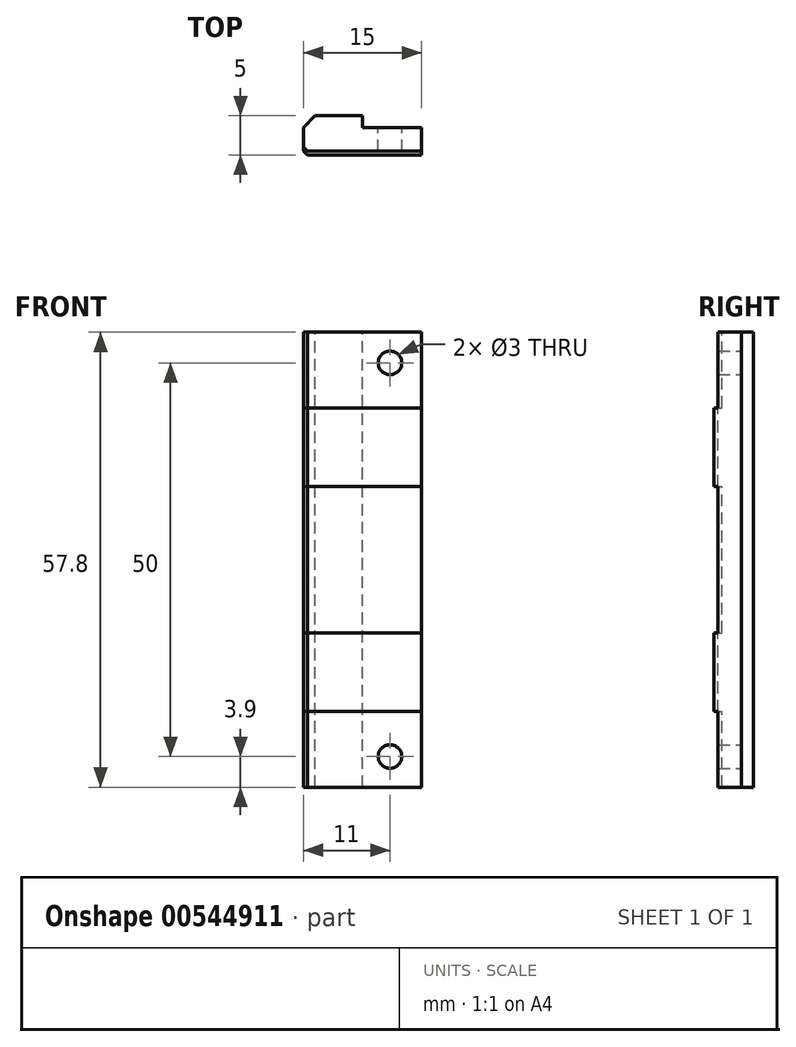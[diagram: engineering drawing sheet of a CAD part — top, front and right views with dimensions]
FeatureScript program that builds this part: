
annotation { "Feature Type Name" : "Feature", "Feature Type Description" : "" }
export const myFeature = defineFeature(function(context is Context, id is Id, definition is map)
    precondition{}
    {
        {
            var Q0;
            Q0=qCreatedBy(makeId("Right.planeOp"),FACE);
            var sketch = newSketch(context, id + "F0", { "sketchPlane" : qUnion([Q0])});
            skLineSegment(sketch, "E0", {"start": v(0, 28.9) * mm, "end": v(3, 28.9) * mm});
            skLineSegment(sketch, "E1", {"start": v(3, 28.9) * mm, "end": v(3, -28.9) * mm});
            skLineSegment(sketch, "E2", {"start": v(3, -28.9) * mm, "end": v(0, -28.9) * mm});
            skLineSegment(sketch, "E3", {"start": v(0, 28.9) * mm, "end": v(0, 24.9) * mm});
            skLineSegment(sketch, "E4", {"start": v(0, 24.9) * mm, "end": v(0, 24.9) * mm});
            skLineSegment(sketch, "E5", {"start": v(0, 24.9) * mm, "end": v(0, -24.9) * mm});
            skLineSegment(sketch, "E6", {"start": v(0, -24.9) * mm, "end": v(0, -24.9) * mm});
            skLineSegment(sketch, "E7", {"start": v(0, -24.9) * mm, "end": v(0, -28.9) * mm});
            skSolve(sketch);
        }
        {
            var Q0;
            Q0=qSketchRegion(id+"F0",true);
            extrude(context, id + "F1", {"entities" : qUnion([Q0]), "depth" : 7.5 * mm, "hasSecondDirection" : true, "secondDirectionOppositeDirection" : true, "secondDirectionDepth" : 7.5 * mm});
        }
        {
            var Q0;
            Q0=makeQuery(id+"F1.opExtrude","SWEPT_FACE",FACE,{"disambiguationData":[OSD([sQuery(id+"F0.wireOp",EDGE,"E1")])]});
            var sketch = newSketch(context, id + "F2", { "sketchPlane" : qUnion([Q0])});
            skCircle(sketch, "E8", {"center": v(-3.5, 25) * mm, "radius": 1.5 * mm});
            skCircle(sketch, "E9", {"center": v(-3.5, -25) * mm, "radius": 1.5 * mm});
            skSolve(sketch);
        }
        {
            var Q0;
            Q0=makeQuery(id+"F1.opExtrude","SWEPT_FACE",FACE,{"disambiguationData":[OSD([sQuery(id+"F0.wireOp",EDGE,"E2")])]});
            var sketch = newSketch(context, id + "F3", { "sketchPlane" : qUnion([Q0])});
            skCircle(sketch, "E10", {"center": v(0, -60) * mm, "radius": 2.5 * mm});
            skSolve(sketch);
        }
        {
            var Q0;
            Q0=qSketchRegion(id+"F3",true);
            extrude(context, id + "F4", {"entities" : qUnion([Q0]), "operationType" : NewBodyOperationType.REMOVE, "oppositeDirection" : true, "depth" : 100 * mm});
        }
        {
            var Q0;
            Q0=makeQuery(id+"F1.opExtrude","SWEPT_FACE",FACE,{"disambiguationData":[OSD([sQuery(id+"F0.wireOp",EDGE,"E1")])]});
            var sketch = newSketch(context, id + "F5", { "sketchPlane" : qUnion([Q0])});
            skCircle(sketch, "E11", {"center": v(-3.5, 31) * mm, "radius": 1.5 * mm});
            skCircle(sketch, "E12", {"center": v(-3.5, -31) * mm, "radius": 1.5 * mm});
            skSolve(sketch);
        }
        {
            var Q0;
            Q0=makeQuery(id+"F1.opExtrude","CAP_FACE",FACE,{"disambiguationData":[OSD([sQuery(id+"F0.wireOp",EDGE,"E0"),sQuery(id+"F0.wireOp",EDGE,"E1"),sQuery(id+"F0.wireOp",EDGE,"E2"),sQuery(id+"F0.wireOp",EDGE,"E3"),sQuery(id+"F0.wireOp",EDGE,"E5"),sQuery(id+"F0.wireOp",EDGE,"E7")])],"isStart":false});
            var sketch = newSketch(context, id + "F6", { "sketchPlane" : qUnion([Q0])});
            skLineSegment(sketch, "E13.bottom", {"start": v(0, 19.29) * mm, "end": v(-0.5, 19.29) * mm});
            skLineSegment(sketch, "E13.top", {"start": v(0, 9.29) * mm, "end": v(-0.5, 9.29) * mm});
            skLineSegment(sketch, "E13.left", {"start": v(0, 19.29) * mm, "end": v(0, 9.29) * mm});
            skLineSegment(sketch, "E13.right", {"start": v(-0.5, 19.29) * mm, "end": v(-0.5, 9.29) * mm});
            skLineSegment(sketch, "E14.bottom", {"start": v(0, -9.29) * mm, "end": v(-0.5, -9.29) * mm});
            skLineSegment(sketch, "E14.top", {"start": v(0, -19.29) * mm, "end": v(-0.5, -19.29) * mm});
            skLineSegment(sketch, "E14.left", {"start": v(0, -9.29) * mm, "end": v(0, -19.29) * mm});
            skLineSegment(sketch, "E14.right", {"start": v(-0.5, -9.29) * mm, "end": v(-0.5, -19.29) * mm});
            skLineSegment(sketch, "E15", {"start": v(-19.13, -14.29) * mm, "end": v(16.5, -14.29) * mm, "construction": true});
            skPoint(sketch, "E15.startSnap0", {"position": v(-0.5, -14.29) * mm});
            skLineSegment(sketch, "E16", {"start": v(-17.07, 14.29) * mm, "end": v(17.48, 14.29) * mm, "construction": true});
            skPoint(sketch, "E16.startSnap0", {"position": v(-0.5, 14.29) * mm});
            skSolve(sketch);
        }
        {
            var Q0;
            Q0=qSketchRegion(id+"F6",true);
            var Q1;
            Q1=makeQuery(id+"F1.opExtrude","CAP_FACE",FACE,{"disambiguationData":[OSD([sQuery(id+"F0.wireOp",EDGE,"E0"),sQuery(id+"F0.wireOp",EDGE,"E1"),sQuery(id+"F0.wireOp",EDGE,"E2"),sQuery(id+"F0.wireOp",EDGE,"E3"),sQuery(id+"F0.wireOp",EDGE,"E5"),sQuery(id+"F0.wireOp",EDGE,"E7")])],"isStart":true});
            extrude(context, id + "F7", {"entities" : qUnion([Q0]), "operationType" : NewBodyOperationType.ADD, "endBound" : BoundingType.UP_TO_SURFACE, "oppositeDirection" : true, "endBoundEntityFace" : qUnion([Q1]), "depth" : 25 * mm});
        }
        {
            var Q0;
            Q0=makeQuery(id+"Fmcx1tmVuyddfUs_2.boolean.opBoolean","MERGE",FACE,{"derivedFrom":[makeQuery(id+"F1.opExtrude","SWEPT_FACE",FACE,{"disambiguationData":[OSD([sQuery(id+"F0.wireOp",EDGE,"E1")])]}),makeQuery(id+"Fmcx1tmVuyddfUs_2.opExtrude","CAP_FACE",FACE,{"disambiguationData":[OSD([sQuery(id+"FtdUe9tOK60J6PF_2.wireOp",EDGE,"JsNW8nu7-rLeb-dfcb-XSDR-FWr7f3ZU8y3m.bottom"),sQuery(id+"FtdUe9tOK60J6PF_2.wireOp",EDGE,"JsNW8nu7-rLeb-dfcb-XSDR-FWr7f3ZU8y3m.top"),sQuery(id+"FtdUe9tOK60J6PF_2.wireOp",EDGE,"JsNW8nu7-rLeb-dfcb-XSDR-FWr7f3ZU8y3m.left"),sQuery(id+"FtdUe9tOK60J6PF_2.wireOp",EDGE,"JsNW8nu7-rLeb-dfcb-XSDR-FWr7f3ZU8y3m.right")])],"isStart":true}),makeQuery(id+"Fmcx1tmVuyddfUs_2.opExtrude","CAP_FACE",FACE,{"disambiguationData":[OSD([sQuery(id+"FtdUe9tOK60J6PF_2.wireOp",EDGE,"ceRr9AZa-OO9h-L4Fo-6wB5-B8ZzmuX6AbRb.bottom"),sQuery(id+"FtdUe9tOK60J6PF_2.wireOp",EDGE,"ceRr9AZa-OO9h-L4Fo-6wB5-B8ZzmuX6AbRb.top"),sQuery(id+"FtdUe9tOK60J6PF_2.wireOp",EDGE,"ceRr9AZa-OO9h-L4Fo-6wB5-B8ZzmuX6AbRb.left"),sQuery(id+"FtdUe9tOK60J6PF_2.wireOp",EDGE,"ceRr9AZa-OO9h-L4Fo-6wB5-B8ZzmuX6AbRb.right")])],"isStart":true})]});
            var sketch = newSketch(context, id + "F8", { "sketchPlane" : qUnion([Q0])});
            skLineSegment(sketch, "E17", {"start": v(0, -35.02) * mm, "end": v(0, 28.9) * mm});
            skSolve(sketch);
        }
        {
            var Q0;
            Q0=qSketchRegion(id+"F2",true);
            extrude(context, id + "F9", {"entities" : qUnion([Q0]), "operationType" : NewBodyOperationType.REMOVE, "oppositeDirection" : true, "depth" : 25 * mm});
        }
        {
            var Q0;
            {var subQ4=sQuery(id+"FtdUe9tOK60J6PF_2.wireOp",EDGE,"JsNW8nu7-rLeb-dfcb-XSDR-FWr7f3ZU8y3m.right");var subQ5=makeQuery(id+"Fmcx1tmVuyddfUs_2.opExtrude","CAP_EDGE",EDGE,{"disambiguationData":[OSD([subQ4])],"isStart":true});Q0=makeQuery(id+"F8.imprint","IMPRINT",FACE,{"disambiguationData":[TD([[makeQuery(id+"F8.imprint","IMPRINT",EDGE,{"derivedFrom":subQ5}),-1.0]])]});}
            var Q1;
            {var subQ1=sQuery(id+"F0.wireOp",EDGE,"E1");var subQ6=makeQuery(id+"F1.opExtrude","CAP_EDGE",EDGE,{"disambiguationData":[OSD([subQ1])],"isStart":true});Q1=makeQuery(id+"F8.imprint","IMPRINT",FACE,{"disambiguationData":[TD([[makeQuery(id+"F8.imprint","IMPRINT",EDGE,{"derivedFrom":subQ6}),-1.0]])]});}
            extrude(context, id + "F10", {"entities" : qUnion([Q0, Q1]), "operationType" : NewBodyOperationType.ADD, "depth" : 1.5 * mm});
        }
        {
            var Q0;
            Q0=makeQuery(id+"F10.opExtrude","CAP_EDGE",EDGE,{"disambiguationData":[OSD([sQuery(id+"FtdUe9tOK60J6PF_2.wireOp",EDGE,"ceRr9AZa-OO9h-L4Fo-6wB5-B8ZzmuX6AbRb.right")])],"isStart":false});
            var Q1;
            {var subQ0=sQuery(id+"FtdUe9tOK60J6PF_2.wireOp",EDGE,"ceRr9AZa-OO9h-L4Fo-6wB5-B8ZzmuX6AbRb.right");var subQ1=sQuery(id+"FtdUe9tOK60J6PF_2.wireOp",EDGE,"ceRr9AZa-OO9h-L4Fo-6wB5-B8ZzmuX6AbRb.left");var subQ2=sQuery(id+"FtdUe9tOK60J6PF_2.wireOp",EDGE,"ceRr9AZa-OO9h-L4Fo-6wB5-B8ZzmuX6AbRb.top");var subQ3=sQuery(id+"FtdUe9tOK60J6PF_2.wireOp",EDGE,"ceRr9AZa-OO9h-L4Fo-6wB5-B8ZzmuX6AbRb.bottom");var subQ4=sQuery(id+"FtdUe9tOK60J6PF_2.wireOp",EDGE,"JsNW8nu7-rLeb-dfcb-XSDR-FWr7f3ZU8y3m.right");var subQ5=sQuery(id+"FtdUe9tOK60J6PF_2.wireOp",EDGE,"JsNW8nu7-rLeb-dfcb-XSDR-FWr7f3ZU8y3m.left");var subQ6=sQuery(id+"FtdUe9tOK60J6PF_2.wireOp",EDGE,"JsNW8nu7-rLeb-dfcb-XSDR-FWr7f3ZU8y3m.top");var subQ7=sQuery(id+"FtdUe9tOK60J6PF_2.wireOp",EDGE,"JsNW8nu7-rLeb-dfcb-XSDR-FWr7f3ZU8y3m.bottom");var subQ8=sQuery(id+"F0.wireOp",EDGE,"E1");Q1=makeQuery(id+"F10.opExtrude","CAP_EDGE",EDGE,{"disambiguationData":[OSD([subQ8,subQ7,subQ6,subQ5,subQ4,subQ3,subQ2,subQ1,subQ0]),TDD([makeQuery(id+"F8.imprint","IMPRINT",EDGE,{"derivedFrom":makeQuery(id+"FqHL6Umb6N44dGH_2.opFillet","BLEND_EDGE",EDGE,{"blendedFrom":[makeQuery(id+"Fmcx1tmVuyddfUs_2.opExtrude","SWEPT_EDGE",EDGE,{"disambiguationData":[OSD([subQ8,subQ2,subQ1])]}),makeQuery(id+"Fmcx1tmVuyddfUs_2.boolean.opBoolean","MERGE",FACE,{"derivedFrom":[makeQuery(id+"F1.opExtrude","SWEPT_FACE",FACE,{"disambiguationData":[OSD([subQ8])]}),makeQuery(id+"Fmcx1tmVuyddfUs_2.opExtrude","CAP_FACE",FACE,{"disambiguationData":[OSD([subQ7,subQ6,subQ5,subQ4])],"isStart":true}),makeQuery(id+"Fmcx1tmVuyddfUs_2.opExtrude","CAP_FACE",FACE,{"disambiguationData":[OSD([subQ3,subQ2,subQ1,subQ0])],"isStart":true})]})],"blendedInto":[makeQuery(id+"Fmcx1tmVuyddfUs_2.boolean.opBoolean","MERGE",FACE,{"derivedFrom":[makeQuery(id+"F1.opExtrude","SWEPT_FACE",FACE,{"disambiguationData":[OSD([subQ8])]}),makeQuery(id+"Fmcx1tmVuyddfUs_2.opExtrude","CAP_FACE",FACE,{"disambiguationData":[OSD([subQ7,subQ6,subQ5,subQ4])],"isStart":true}),makeQuery(id+"Fmcx1tmVuyddfUs_2.opExtrude","CAP_FACE",FACE,{"disambiguationData":[OSD([subQ3,subQ2,subQ1,subQ0])],"isStart":true})]})]})})])],"isStart":false});}
            var Q2;
            Q2=makeQuery(id+"F10.opExtrude","CAP_EDGE",EDGE,{"disambiguationData":[OSD([sQuery(id+"F0.wireOp",EDGE,"E1")])],"isStart":false});
            var Q3;
            {var subQ0=sQuery(id+"FtdUe9tOK60J6PF_2.wireOp",EDGE,"ceRr9AZa-OO9h-L4Fo-6wB5-B8ZzmuX6AbRb.right");var subQ1=sQuery(id+"FtdUe9tOK60J6PF_2.wireOp",EDGE,"ceRr9AZa-OO9h-L4Fo-6wB5-B8ZzmuX6AbRb.left");var subQ2=sQuery(id+"FtdUe9tOK60J6PF_2.wireOp",EDGE,"ceRr9AZa-OO9h-L4Fo-6wB5-B8ZzmuX6AbRb.top");var subQ3=sQuery(id+"FtdUe9tOK60J6PF_2.wireOp",EDGE,"ceRr9AZa-OO9h-L4Fo-6wB5-B8ZzmuX6AbRb.bottom");var subQ4=sQuery(id+"FtdUe9tOK60J6PF_2.wireOp",EDGE,"JsNW8nu7-rLeb-dfcb-XSDR-FWr7f3ZU8y3m.right");var subQ5=sQuery(id+"FtdUe9tOK60J6PF_2.wireOp",EDGE,"JsNW8nu7-rLeb-dfcb-XSDR-FWr7f3ZU8y3m.left");var subQ6=sQuery(id+"FtdUe9tOK60J6PF_2.wireOp",EDGE,"JsNW8nu7-rLeb-dfcb-XSDR-FWr7f3ZU8y3m.top");var subQ7=sQuery(id+"FtdUe9tOK60J6PF_2.wireOp",EDGE,"JsNW8nu7-rLeb-dfcb-XSDR-FWr7f3ZU8y3m.bottom");var subQ8=sQuery(id+"F0.wireOp",EDGE,"E1");Q3=makeQuery(id+"F10.opExtrude","CAP_EDGE",EDGE,{"disambiguationData":[OSD([subQ8,subQ7,subQ6,subQ5,subQ4,subQ3,subQ2,subQ1,subQ0]),TDD([makeQuery(id+"F8.imprint","IMPRINT",EDGE,{"derivedFrom":makeQuery(id+"FqHL6Umb6N44dGH_2.opFillet","BLEND_EDGE",EDGE,{"blendedFrom":[makeQuery(id+"Fmcx1tmVuyddfUs_2.opExtrude","SWEPT_EDGE",EDGE,{"disambiguationData":[OSD([subQ8,subQ6,subQ5])]}),makeQuery(id+"Fmcx1tmVuyddfUs_2.boolean.opBoolean","MERGE",FACE,{"derivedFrom":[makeQuery(id+"F1.opExtrude","SWEPT_FACE",FACE,{"disambiguationData":[OSD([subQ8])]}),makeQuery(id+"Fmcx1tmVuyddfUs_2.opExtrude","CAP_FACE",FACE,{"disambiguationData":[OSD([subQ7,subQ6,subQ5,subQ4])],"isStart":true}),makeQuery(id+"Fmcx1tmVuyddfUs_2.opExtrude","CAP_FACE",FACE,{"disambiguationData":[OSD([subQ3,subQ2,subQ1,subQ0])],"isStart":true})]})],"blendedInto":[makeQuery(id+"Fmcx1tmVuyddfUs_2.boolean.opBoolean","MERGE",FACE,{"derivedFrom":[makeQuery(id+"F1.opExtrude","SWEPT_FACE",FACE,{"disambiguationData":[OSD([subQ8])]}),makeQuery(id+"Fmcx1tmVuyddfUs_2.opExtrude","CAP_FACE",FACE,{"disambiguationData":[OSD([subQ7,subQ6,subQ5,subQ4])],"isStart":true}),makeQuery(id+"Fmcx1tmVuyddfUs_2.opExtrude","CAP_FACE",FACE,{"disambiguationData":[OSD([subQ3,subQ2,subQ1,subQ0])],"isStart":true})]})]})})])],"isStart":false});}
            var Q4;
            Q4=makeQuery(id+"F10.opExtrude","CAP_EDGE",EDGE,{"disambiguationData":[OSD([sQuery(id+"FtdUe9tOK60J6PF_2.wireOp",EDGE,"JsNW8nu7-rLeb-dfcb-XSDR-FWr7f3ZU8y3m.top")])],"isStart":false});
            var Q5;
            Q5=makeQuery(id+"F10.opExtrude","CAP_EDGE",EDGE,{"disambiguationData":[OSD([sQuery(id+"FtdUe9tOK60J6PF_2.wireOp",EDGE,"JsNW8nu7-rLeb-dfcb-XSDR-FWr7f3ZU8y3m.right")])],"isStart":false});
            var Q6;
            Q6=makeQuery(id+"F10.opExtrude","CAP_EDGE",EDGE,{"disambiguationData":[OSD([sQuery(id+"FtdUe9tOK60J6PF_2.wireOp",EDGE,"ceRr9AZa-OO9h-L4Fo-6wB5-B8ZzmuX6AbRb.top")])],"isStart":false});
            chamfer(context, id + "F11", {"entities" : qUnion([Q0, Q1, Q2, Q3, Q4, Q5, Q6]), "width" : 1.5 * mm, "tangentPropagation" : true});
        }
        {
            var Q0;
            Q0=qSketchRegion(id+"F5",true);
            extrude(context, id + "F12", {"entities" : qUnion([Q0]), "operationType" : NewBodyOperationType.REMOVE, "oppositeDirection" : true, "depth" : 25 * mm});
        }
        {
            var Q0;
            {var subQ0=sQuery(id+"F6.wireOp",EDGE,"E13.top");var subQ1=sQuery(id+"F0.wireOp",EDGE,"E7");var subQ2=sQuery(id+"F0.wireOp",EDGE,"E5");var subQ3=sQuery(id+"F0.wireOp",EDGE,"E3");Q0=makeQuery(id+"F7.boolean.opBoolean","SPLIT",EDGE,{"disambiguationData":[TD([makeQuery(id+"F7.opExtrude","SWEPT_FACE",FACE,{"disambiguationData":[OSD([subQ0])]})])],"derivedFrom":makeQuery(id+"F1.opExtrude","CAP_EDGE",EDGE,{"disambiguationData":[OSD([subQ3,subQ2,subQ1])],"isStart":true})});}
            var Q1;
            Q1=makeQuery(id+"F7.opExtrude","CAP_EDGE",EDGE,{"disambiguationData":[OSD([sQuery(id+"F6.wireOp",EDGE,"E13.right")])],"isStart":false});
            var Q2;
            {var subQ1=sQuery(id+"F0.wireOp",EDGE,"E7");var subQ2=sQuery(id+"F0.wireOp",EDGE,"E5");var subQ3=sQuery(id+"F0.wireOp",EDGE,"E3");var subQ4=sQuery(id+"F0.wireOp",EDGE,"E0");Q2=makeQuery(id+"F7.boolean.opBoolean","SPLIT",EDGE,{"disambiguationData":[TD([makeQuery(id+"F1.opExtrude","SWEPT_FACE",FACE,{"disambiguationData":[OSD([subQ4])]})])],"derivedFrom":makeQuery(id+"F1.opExtrude","CAP_EDGE",EDGE,{"disambiguationData":[OSD([subQ3,subQ2,subQ1])],"isStart":true})});}
            var Q3;
            Q3=makeQuery(id+"F7.opExtrude","CAP_EDGE",EDGE,{"disambiguationData":[OSD([sQuery(id+"F6.wireOp",EDGE,"E14.right")])],"isStart":false});
            var Q4;
            {var subQ0=sQuery(id+"F0.wireOp",EDGE,"E7");var subQ1=sQuery(id+"F0.wireOp",EDGE,"E5");var subQ2=sQuery(id+"F0.wireOp",EDGE,"E3");var subQ4=sQuery(id+"F0.wireOp",EDGE,"E2");Q4=makeQuery(id+"F7.boolean.opBoolean","SPLIT",EDGE,{"disambiguationData":[TD([makeQuery(id+"F1.opExtrude","SWEPT_FACE",FACE,{"disambiguationData":[OSD([subQ4])]})])],"derivedFrom":makeQuery(id+"F1.opExtrude","CAP_EDGE",EDGE,{"disambiguationData":[OSD([subQ2,subQ1,subQ0])],"isStart":true})});}
            chamfer(context, id + "F13", {"entities" : qUnion([Q0, Q1, Q2, Q3, Q4]), "width" : 0.5 * mm, "tangentPropagation" : true});
        }
    });
